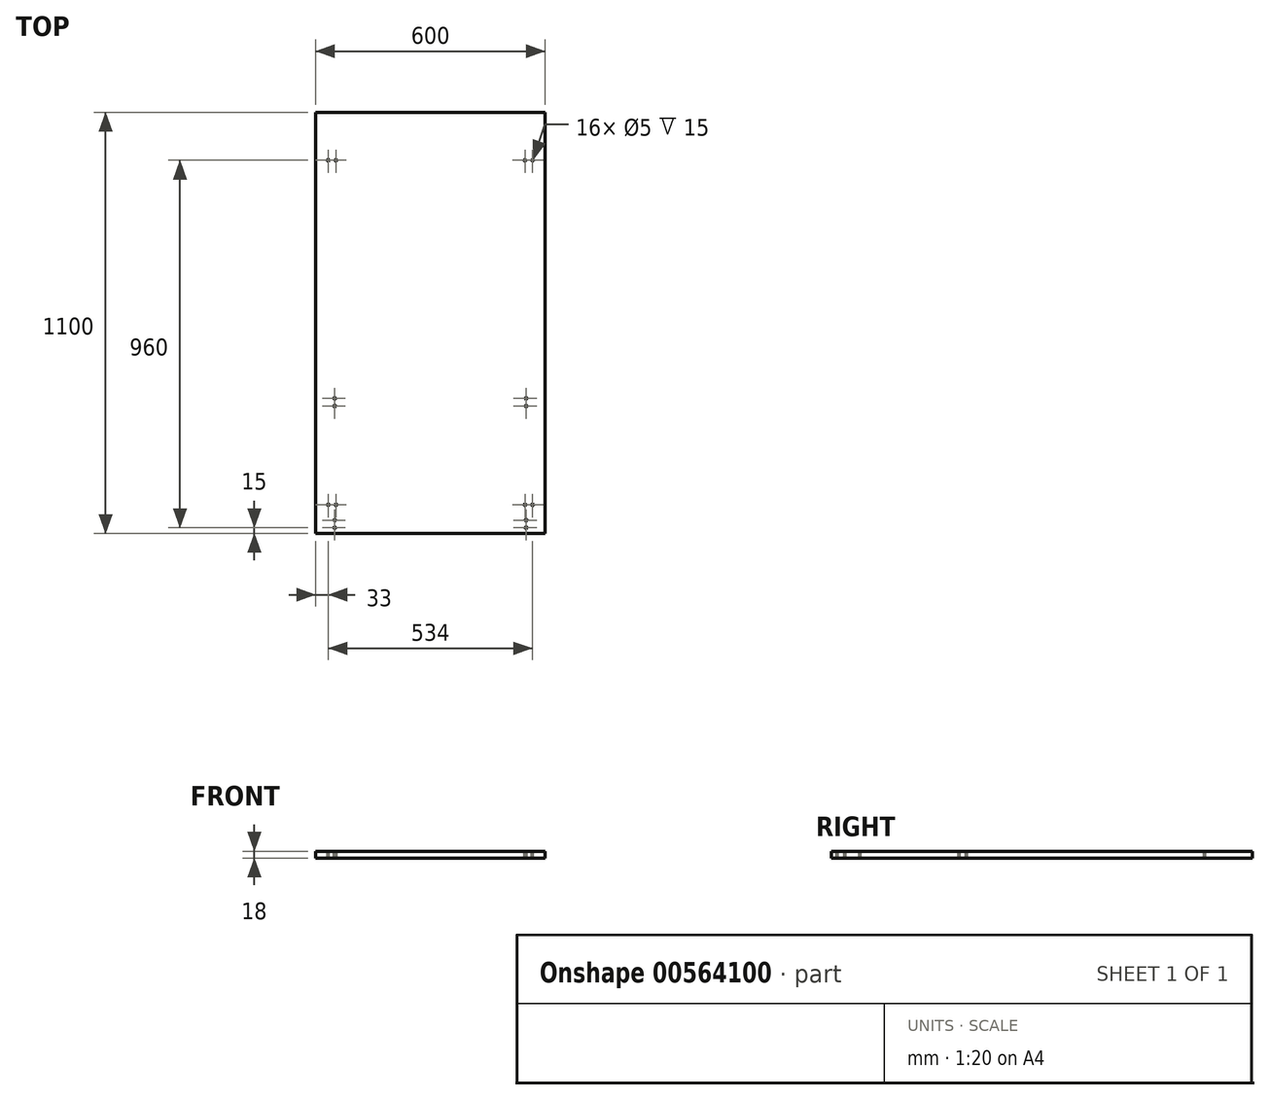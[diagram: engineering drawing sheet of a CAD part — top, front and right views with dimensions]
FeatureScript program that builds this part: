
annotation { "Feature Type Name" : "Feature", "Feature Type Description" : "" }
export const myFeature = defineFeature(function(context is Context, id is Id, definition is map)
    precondition{}
    {
        {
            var Q0;
            Q0=qCreatedBy(makeId("Top.planeOp"),FACE);
            var sketch = newSketch(context, id + "F0", { "sketchPlane" : qUnion([Q0])});
            skLineSegment(sketch, "E0.bottom", {"start": v(-300, 550) * mm, "end": v(300, 550) * mm});
            skLineSegment(sketch, "E0.top", {"start": v(-300, -550) * mm, "end": v(300, -550) * mm});
            skLineSegment(sketch, "E0.left", {"start": v(-300, 550) * mm, "end": v(-300, -550) * mm});
            skLineSegment(sketch, "E0.right", {"start": v(300, 550) * mm, "end": v(300, -550) * mm});
            skSolve(sketch);
        }
        {
            var Q0;
            Q0=makeQuery(id+"F0.imprint","IMPRINT",FACE,{"disambiguationData":[TD([[makeQuery(id+"F0.imprint","IMPRINT",EDGE,{"derivedFrom":sQuery(id+"F0.wireOp",EDGE,"E0.bottom")}),-1.0]])]});
            extrude(context, id + "F1", {"entities" : qUnion([Q0]), "depth" : 18 * mm, "offsetDistance" : 25.4 * mm});
        }
        {
            var Q0;
            Q0=makeQuery(id+"F1.opExtrude","CAP_FACE",FACE,{"disambiguationData":[OSD([sQuery(id+"F0.wireOp",EDGE,"E0.bottom"),sQuery(id+"F0.wireOp",EDGE,"E0.top"),sQuery(id+"F0.wireOp",EDGE,"E0.left"),sQuery(id+"F0.wireOp",EDGE,"E0.right")])],"isStart":false});
            var sketch = newSketch(context, id + "F2", { "sketchPlane" : qUnion([Q0])});
            skCircle(sketch, "E1", {"center": v(247, -475) * mm, "radius": 2.5 * mm});
            skCircle(sketch, "E2", {"center": v(267, -475) * mm, "radius": 2.5 * mm});
            skCircle(sketch, "E3", {"center": v(250, -217) * mm, "radius": 2.5 * mm});
            skCircle(sketch, "E4", {"center": v(250, -197) * mm, "radius": 2.5 * mm});
            skCircle(sketch, "E5", {"center": v(267, 425) * mm, "radius": 2.5 * mm});
            skCircle(sketch, "E6", {"center": v(247, 425) * mm, "radius": 2.5 * mm});
            skCircle(sketch, "E7.MirrorC", {"center": v(-247, 425) * mm, "radius": 2.5 * mm});
            skCircle(sketch, "E8.MirrorC", {"center": v(-267, 425) * mm, "radius": 2.5 * mm});
            skCircle(sketch, "E9.MirrorC", {"center": v(-250, -197) * mm, "radius": 2.5 * mm});
            skCircle(sketch, "E10.MirrorC", {"center": v(-250, -217) * mm, "radius": 2.5 * mm});
            skCircle(sketch, "E11.MirrorC", {"center": v(-267, -475) * mm, "radius": 2.5 * mm});
            skCircle(sketch, "E12.MirrorC", {"center": v(-247, -475) * mm, "radius": 2.5 * mm});
            skCircle(sketch, "E13", {"center": v(250, -515) * mm, "radius": 2.5 * mm});
            skCircle(sketch, "E14", {"center": v(250, -535) * mm, "radius": 2.5 * mm});
            skCircle(sketch, "E15.MirrorC", {"center": v(-250, -535) * mm, "radius": 2.5 * mm});
            skCircle(sketch, "E16.MirrorC", {"center": v(-250, -515) * mm, "radius": 2.5 * mm});
            skSolve(sketch);
        }
        {
            var Q0;
            Q0 = qSketchRegion(id + "F2", true);
            extrude(context, id + "F3", {"entities" : qUnion([Q0]), "operationType" : NewBodyOperationType.REMOVE, "oppositeDirection" : true, "depth" : 15 * mm, "offsetDistance" : 25 * mm});
        }
    });
